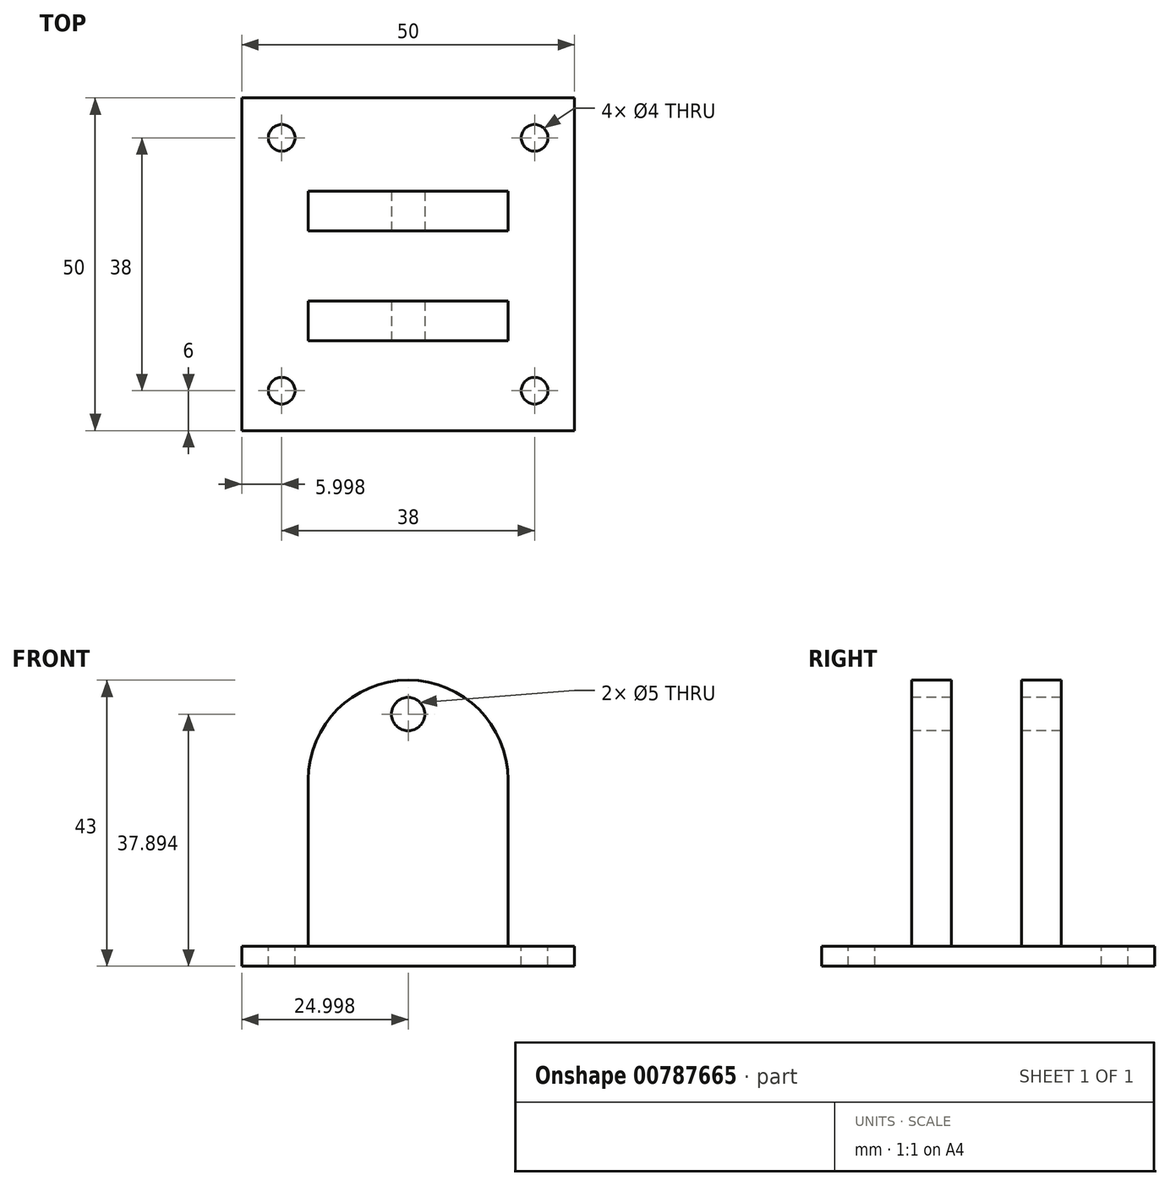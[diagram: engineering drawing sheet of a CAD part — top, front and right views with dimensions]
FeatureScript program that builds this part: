
annotation { "Feature Type Name" : "Feature", "Feature Type Description" : "" }
export const myFeature = defineFeature(function(context is Context, id is Id, definition is map)
    precondition{}
    {
        {
            var Q0;
            Q0=qCreatedBy(makeId("Top.planeOp"),FACE);
            var sketch = newSketch(context, id + "F0", { "sketchPlane" : qUnion([Q0])});
            skLineSegment(sketch, "E0.bottom", {"start": v(-23.83, 27.47) * mm, "end": v(26.17, 27.47) * mm});
            skLineSegment(sketch, "E0.top", {"start": v(-23.83, -22.53) * mm, "end": v(26.17, -22.53) * mm});
            skLineSegment(sketch, "E0.left", {"start": v(-23.83, 27.47) * mm, "end": v(-23.83, -22.53) * mm});
            skLineSegment(sketch, "E0.right", {"start": v(26.17, 27.47) * mm, "end": v(26.17, -22.53) * mm});
            skSolve(sketch);
        }
        {
            var Q0;
            Q0=makeQuery(id+"F0.imprint","IMPRINT",FACE,{"disambiguationData":[TD([[makeQuery(id+"F0.imprint","IMPRINT",EDGE,{"derivedFrom":sQuery(id+"F0.wireOp",EDGE,"E0.bottom")}),-1.0]])]});
            extrude(context, id + "F1", {"entities" : qUnion([Q0]), "depth" : 3 * mm, "offsetDistance" : 25 * mm});
        }
        {
            var Q0;
            Q0=makeQuery(id+"F1.opExtrude","CAP_FACE",FACE,{"disambiguationData":[OSD([sQuery(id+"F0.wireOp",EDGE,"E0.bottom"),sQuery(id+"F0.wireOp",EDGE,"E0.top"),sQuery(id+"F0.wireOp",EDGE,"E0.left"),sQuery(id+"F0.wireOp",EDGE,"E0.right")])],"isStart":false});
            var sketch = newSketch(context, id + "F2", { "sketchPlane" : qUnion([Q0])});
            skLineSegment(sketch, "E1.bottom", {"start": v(-13.83, 13.97) * mm, "end": v(16.17, 13.97) * mm});
            skLineSegment(sketch, "E1.top", {"start": v(-13.83, 7.97) * mm, "end": v(16.17, 7.97) * mm});
            skLineSegment(sketch, "E1.left", {"start": v(-13.83, 13.97) * mm, "end": v(-13.83, 7.97) * mm});
            skLineSegment(sketch, "E1.right", {"start": v(16.17, 13.97) * mm, "end": v(16.17, 7.97) * mm});
            skLineSegment(sketch, "E2.bottom", {"start": v(-13.83, -3.03) * mm, "end": v(16.17, -3.03) * mm});
            skLineSegment(sketch, "E2.top", {"start": v(-13.83, -9.03) * mm, "end": v(16.17, -9.03) * mm});
            skLineSegment(sketch, "E2.left", {"start": v(-13.83, -3.03) * mm, "end": v(-13.83, -9.03) * mm});
            skLineSegment(sketch, "E2.right", {"start": v(16.17, -3.03) * mm, "end": v(16.17, -9.03) * mm});
            skSolve(sketch);
        }
        {
            var Q0;
            Q0=makeQuery(id+"F2.imprint","IMPRINT",FACE,{"disambiguationData":[TD([[makeQuery(id+"F2.imprint","IMPRINT",EDGE,{"derivedFrom":sQuery(id+"F2.wireOp",EDGE,"E2.bottom")}),-1.0]])]});
            extrude(context, id + "F3", {"entities" : qUnion([Q0]), "operationType" : NewBodyOperationType.ADD, "depth" : 40 * mm, "offsetDistance" : 25 * mm});
        }
        {
            var Q0;
            Q0=makeQuery(id+"F1.opExtrude","CAP_FACE",FACE,{"disambiguationData":[OSD([sQuery(id+"F0.wireOp",EDGE,"E0.bottom"),sQuery(id+"F0.wireOp",EDGE,"E0.top"),sQuery(id+"F0.wireOp",EDGE,"E0.left"),sQuery(id+"F0.wireOp",EDGE,"E0.right")])],"isStart":false});
            var sketch = newSketch(context, id + "F4", { "sketchPlane" : qUnion([Q0])});
            skLineSegment(sketch, "E3.bottom", {"start": v(-13.83, 13.47) * mm, "end": v(16.17, 13.47) * mm});
            skLineSegment(sketch, "E3.top", {"start": v(-13.83, 7.47) * mm, "end": v(16.17, 7.47) * mm});
            skLineSegment(sketch, "E3.left", {"start": v(-13.83, 13.47) * mm, "end": v(-13.83, 7.47) * mm});
            skLineSegment(sketch, "E3.right", {"start": v(16.17, 13.47) * mm, "end": v(16.17, 7.47) * mm});
            skSolve(sketch);
        }
        {
            var Q0;
            Q0=makeQuery(id+"F4.imprint","IMPRINT",FACE,{"disambiguationData":[TD([[makeQuery(id+"F4.imprint","IMPRINT",EDGE,{"derivedFrom":sQuery(id+"F4.wireOp",EDGE,"E3.bottom")}),-1.0]])]});
            extrude(context, id + "F5", {"entities" : qUnion([Q0]), "operationType" : NewBodyOperationType.ADD, "depth" : 40 * mm, "offsetDistance" : 25 * mm});
        }
        {
            var Q0;
            Q0=makeQuery(id+"F3.opExtrude","CAP_EDGE",EDGE,{"disambiguationData":[OSD([sQuery(id+"F2.wireOp",EDGE,"E2.left")])],"isStart":false});
            var Q1;
            Q1=makeQuery(id+"F3.opExtrude","CAP_EDGE",EDGE,{"disambiguationData":[OSD([sQuery(id+"F2.wireOp",EDGE,"E2.right")])],"isStart":false});
            fillet(context, id + "F6", {"entities" : qUnion([Q0, Q1]), "radius" : 15 * mm, "tangentPropagation" : true, "allowEdgeOverflow" : false});
        }
        {
            var Q0;
            Q0=makeQuery(id+"F5.opExtrude","CAP_EDGE",EDGE,{"disambiguationData":[OSD([sQuery(id+"F4.wireOp",EDGE,"E3.right")])],"isStart":false});
            var Q1;
            Q1=makeQuery(id+"F5.opExtrude","CAP_EDGE",EDGE,{"disambiguationData":[OSD([sQuery(id+"F4.wireOp",EDGE,"E3.left")])],"isStart":false});
            fillet(context, id + "F7", {"entities" : qUnion([Q0, Q1]), "radius" : 15 * mm, "tangentPropagation" : true, "allowEdgeOverflow" : false});
        }
        {
            var Q0;
            Q0=makeQuery(id+"F3.opExtrude","SWEPT_FACE",FACE,{"disambiguationData":[OSD([sQuery(id+"F2.wireOp",EDGE,"E2.top")])]});
            var sketch = newSketch(context, id + "F8", { "sketchPlane" : qUnion([Q0])});
            skPoint(sketch, "E4", {"position": v(1.17, 37.9) * mm});
            skPoint(sketch, "E4.positionSnap0", {"position": v(1.17, 50) * mm});
            skSolve(sketch);
        }
        {
            var Q0;
            Q0=sQuery(id+"F8.wireOp",VERTEX,"E4");
            var Q1;
            Q1=makeQuery(id+"F1.opExtrude","SWEPT_BODY",BODY,{"disambiguationData":[OSD([sQuery(id+"F0.wireOp",EDGE,"E0.bottom"),sQuery(id+"F0.wireOp",EDGE,"E0.top"),sQuery(id+"F0.wireOp",EDGE,"E0.left"),sQuery(id+"F0.wireOp",EDGE,"E0.right")])]});
            hole(context, id + "F9", {"style" : HoleStyle.SIMPLE, "endStyle" : HoleEndStyle.THROUGH, "holeDiameter" : 5 * mm, "majorDiameter" : 5 * mm, "isTappedThrough" : true, "tappedDepth" : 12 * mm, "tapClearance" : 3, "locations" : qUnion([Q0]), "scope" : qUnion([Q1])});
        }
        {
            var Q0;
            Q0=makeQuery(id+"F1.opExtrude","CAP_FACE",FACE,{"disambiguationData":[OSD([sQuery(id+"F0.wireOp",EDGE,"E0.bottom"),sQuery(id+"F0.wireOp",EDGE,"E0.top"),sQuery(id+"F0.wireOp",EDGE,"E0.left"),sQuery(id+"F0.wireOp",EDGE,"E0.right")])],"isStart":false});
            var sketch = newSketch(context, id + "F10", { "sketchPlane" : qUnion([Q0])});
            skLineSegment(sketch, "E5", {"start": v(0, 7.47) * mm, "end": v(0, -3.03) * mm});
            skSolve(sketch);
        }
        {
            var Q0;
            Q0=makeQuery(id+"F10.imprint","IMPRINT",FACE,{"disambiguationData":[TD([[makeQuery(id+"F10.imprint","IMPRINT",EDGE,{"derivedFrom":makeQuery(id+"F1.opExtrude","CAP_EDGE",EDGE,{"disambiguationData":[OSD([sQuery(id+"F0.wireOp",EDGE,"E0.bottom")])],"isStart":false})}),-1.0]])]});
            var sketch = newSketch(context, id + "F11", { "sketchPlane" : qUnion([Q0])});
            skPoint(sketch, "E6", {"position": v(-17.83, 21.47) * mm});
            skPoint(sketch, "E7", {"position": v(20.17, 21.47) * mm});
            skPoint(sketch, "E8", {"position": v(20.17, -16.53) * mm});
            skPoint(sketch, "E9", {"position": v(-17.83, -16.53) * mm});
            skSolve(sketch);
        }
        {
            var Q0;
            Q0=sQuery(id+"F11.wireOp",VERTEX,"E6");
            var Q1;
            Q1=sQuery(id+"F11.wireOp",VERTEX,"E7");
            var Q2;
            Q2=sQuery(id+"F11.wireOp",VERTEX,"E8");
            var Q3;
            Q3=sQuery(id+"F11.wireOp",VERTEX,"E9");
            var Q4;
            Q4=makeQuery(id+"F1.opExtrude","SWEPT_BODY",BODY,{"disambiguationData":[OSD([sQuery(id+"F0.wireOp",EDGE,"E0.bottom"),sQuery(id+"F0.wireOp",EDGE,"E0.top"),sQuery(id+"F0.wireOp",EDGE,"E0.left"),sQuery(id+"F0.wireOp",EDGE,"E0.right")])]});
            hole(context, id + "F12", {"style" : HoleStyle.SIMPLE, "endStyle" : HoleEndStyle.BLIND, "holeDiameter" : 4 * mm, "majorDiameter" : 5 * mm, "holeDepth" : 15 * mm, "isTappedThrough" : true, "tappedDepth" : 12 * mm, "tapClearance" : 3, "locations" : qUnion([Q0, Q1, Q2, Q3]), "scope" : qUnion([Q4])});
        }
    });
